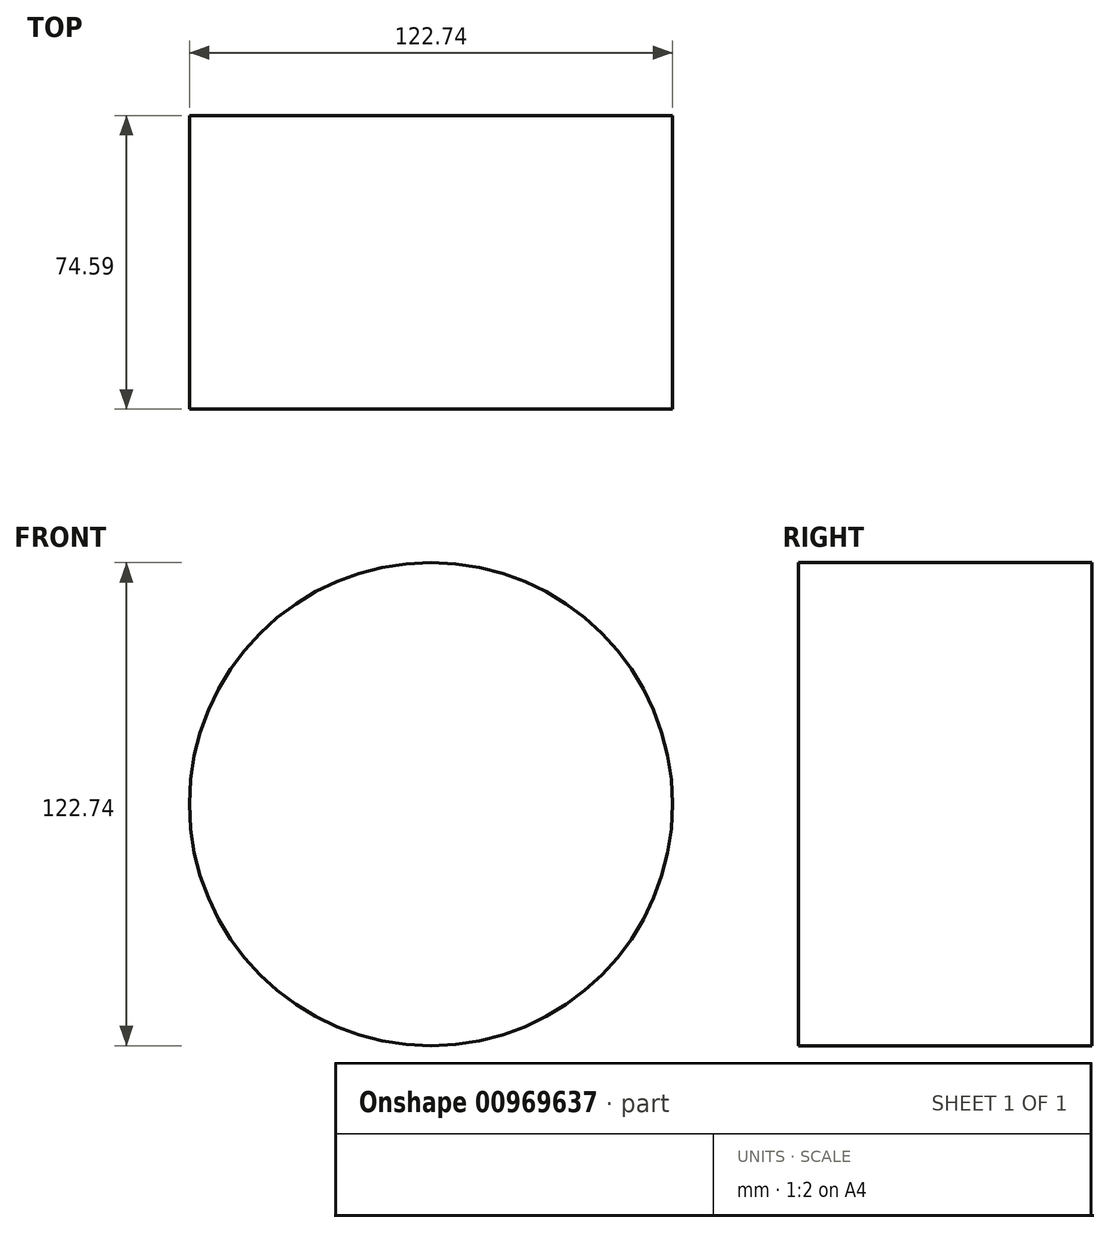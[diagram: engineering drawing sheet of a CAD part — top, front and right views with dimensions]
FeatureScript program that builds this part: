
annotation { "Feature Type Name" : "Feature", "Feature Type Description" : "" }
export const myFeature = defineFeature(function(context is Context, id is Id, definition is map)
    precondition{}
    {
        {
            var Q0;
            Q0=qCreatedBy(makeId("Front.planeOp"),FACE);
            var sketch = newSketch(context, id + "F0", { "sketchPlane" : qUnion([Q0])});
            skCircle(sketch, "E0", {"center": v(0, 0) * mm, "radius": 61.37 * mm});
            skSolve(sketch);
        }
        {
            var Q0;
            Q0=makeQuery(id+"F0.imprint","IMPRINT",FACE,{"disambiguationData":[TD([[makeQuery(id+"F0.imprint","IMPRINT",EDGE,{"derivedFrom":sQuery(id+"F0.wireOp",EDGE,"E0")}),1.0]])]});
            extrude(context, id + "F1", {"entities" : qUnion([Q0]), "depth" : 74.6 * mm, "offsetDistance" : 25 * mm});
        }
    });
